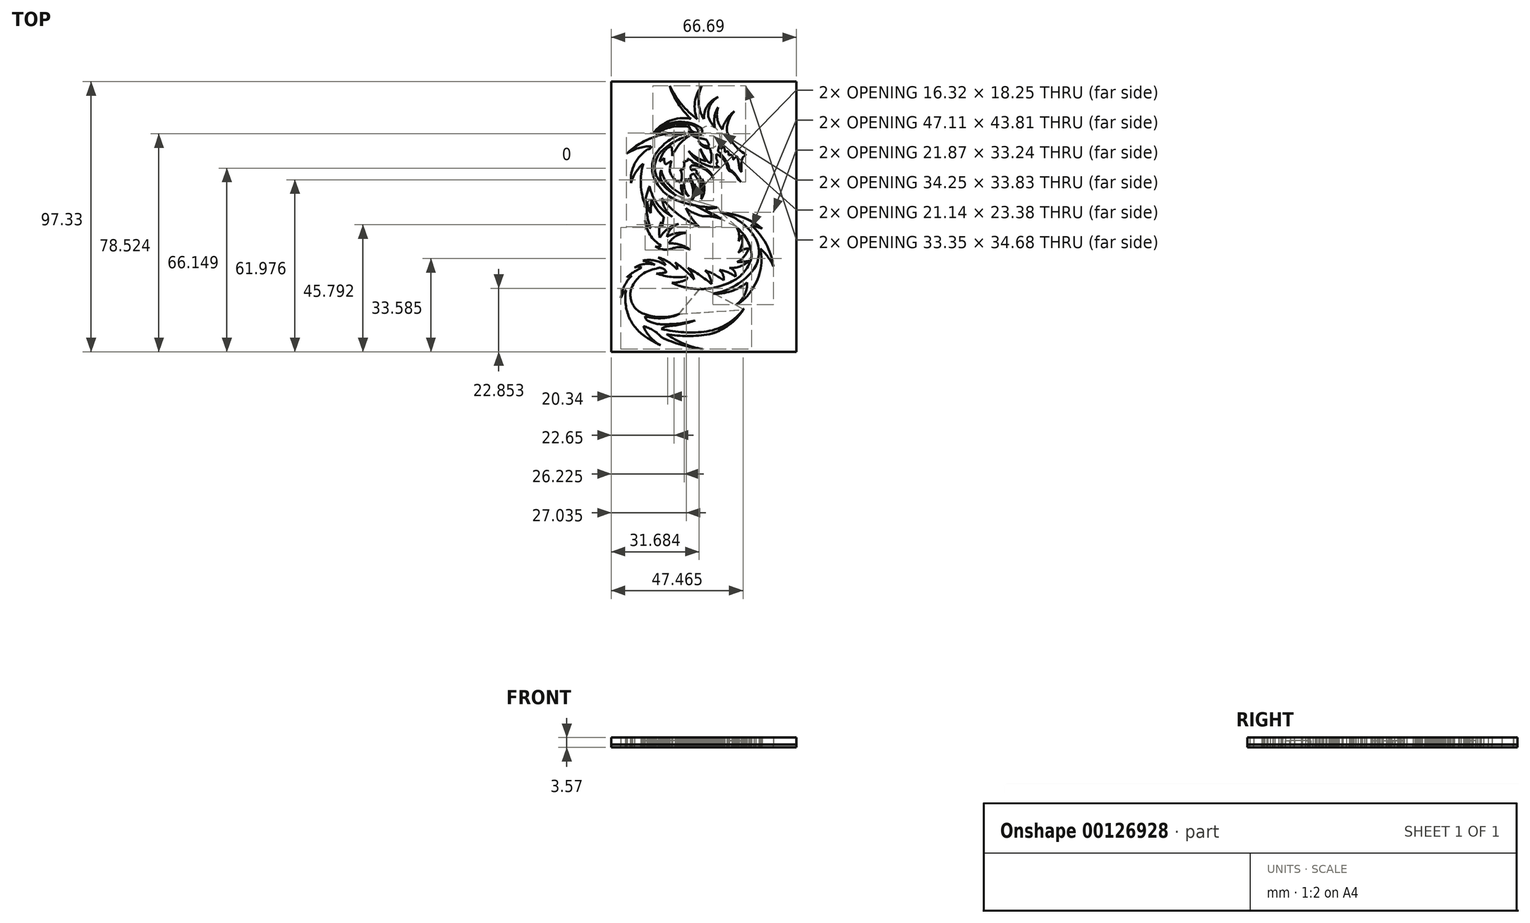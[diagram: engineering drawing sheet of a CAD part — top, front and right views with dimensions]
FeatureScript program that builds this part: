
annotation { "Feature Type Name" : "Feature", "Feature Type Description" : "" }
export const myFeature = defineFeature(function(context is Context, id is Id, definition is map)
    precondition{}
    {
        {
            var Q0;
            Q0=qCreatedBy(makeId("Top.planeOp"),FACE);
            var sketch = newSketch(context, id + "F0", { "sketchPlane" : qUnion([Q0])});
            skArc(sketch, "E0", {"start": v(-30.65, 39.22) * mm, "mid": v(-28.15, 34.33) * mm, "end": v(-23.98, 30.75) * mm});
            skArc(sketch, "E1", {"start": v(-27.91, 46.24) * mm, "mid": v(-29.97, 43) * mm, "end": v(-30.65, 39.22) * mm});
            skArc(sketch, "E2", {"start": v(-27.91, 46.24) * mm, "mid": v(-30.67, 43.35) * mm, "end": v(-32.32, 39.7) * mm});
            skArc(sketch, "E3", {"start": v(-33.8, 47.63) * mm, "mid": v(-34.11, 43.47) * mm, "end": v(-32.32, 39.7) * mm});
            skArc(sketch, "E4", {"start": v(-33.8, 47.63) * mm, "mid": v(-35.12, 44.08) * mm, "end": v(-34.92, 40.3) * mm});
            skArc(sketch, "E5", {"start": v(-37.4, 44.6) * mm, "mid": v(-36.44, 42.3) * mm, "end": v(-34.92, 40.3) * mm});
            skArc(sketch, "E6", {"start": v(-33.82, 51.28) * mm, "mid": v(-36.58, 48.47) * mm, "end": v(-37.4, 44.6) * mm});
            skArc(sketch, "E7", {"start": v(-33.82, 51.28) * mm, "mid": v(-37.67, 48.18) * mm, "end": v(-38.9, 43.4) * mm});
            skArc(sketch, "E8", {"start": v(-39.73, 55.3) * mm, "mid": v(-40.83, 49.25) * mm, "end": v(-38.9, 43.4) * mm});
            skArc(sketch, "E9", {"start": v(-39.73, 55.3) * mm, "mid": v(-42.15, 49.52) * mm, "end": v(-41.34, 43.3) * mm});
            skArc(sketch, "E10", {"start": v(-51.25, 55.4) * mm, "mid": v(-47, 48.77) * mm, "end": v(-41.34, 43.3) * mm});
            skArc(sketch, "E11", {"start": v(-51.25, 55.4) * mm, "mid": v(-48.2, 48.97) * mm, "end": v(-43.64, 43.52) * mm});
            skArc(sketch, "E12", {"start": v(-43.64, 43.52) * mm, "mid": v(-51.25, 42.81) * mm, "end": v(-57.28, 38.12) * mm});
            skArc(sketch, "E13", {"start": v(-40.35, 40.47) * mm, "mid": v(-49.23, 42.31) * mm, "end": v(-57.28, 38.12) * mm});
            skArc(sketch, "E14", {"start": v(-41.33, 37.48) * mm, "mid": v(-39.58, 38.56) * mm, "end": v(-40.35, 40.47) * mm});
            skArc(sketch, "E15", {"start": v(-44.38, 38.98) * mm, "mid": v(-42.91, 38.11) * mm, "end": v(-41.33, 37.48) * mm});
            skArc(sketch, "E16", {"start": v(-44.38, 38.98) * mm, "mid": v(-42.8, 37.4) * mm, "end": v(-40.77, 36.48) * mm});
            skArc(sketch, "E17", {"start": v(-37.91, 35.86) * mm, "mid": v(-39.31, 36.3) * mm, "end": v(-40.77, 36.48) * mm});
            skArc(sketch, "E18", {"start": v(-37.01, 33.75) * mm, "mid": v(-37.4, 34.83) * mm, "end": v(-37.91, 35.86) * mm});
            skArc(sketch, "E19", {"start": v(-40.85, 35.6) * mm, "mid": v(-39.24, 34.04) * mm, "end": v(-37.01, 33.75) * mm});
            skArc(sketch, "E20", {"start": v(-40.85, 35.6) * mm, "mid": v(-39.3, 33.56) * mm, "end": v(-36.83, 32.89) * mm});
            skArc(sketch, "E21", {"start": v(-44.1, 40.51) * mm, "mid": v(-50.54, 40.52) * mm, "end": v(-56.45, 37.97) * mm});
            skArc(sketch, "E22", {"start": v(-44.1, 40.51) * mm, "mid": v(-42.88, 38.87) * mm, "end": v(-40.83, 38.7) * mm});
            skArc(sketch, "E23", {"start": v(-40.83, 38.7) * mm, "mid": v(-41.92, 40.55) * mm, "end": v(-43.82, 41.54) * mm});
            skArc(sketch, "E24", {"start": v(-43.82, 41.54) * mm, "mid": v(-50.56, 41.26) * mm, "end": v(-56.45, 37.97) * mm});
            skArc(sketch, "E25", {"start": v(-36.45, 27.58) * mm, "mid": v(-36.2, 30.27) * mm, "end": v(-36.83, 32.89) * mm});
            skArc(sketch, "E26", {"start": v(-37.87, 28.52) * mm, "mid": v(-37.26, 27.9) * mm, "end": v(-36.45, 27.58) * mm});
            skArc(sketch, "E27", {"start": v(-40.23, 32.6) * mm, "mid": v(-39.08, 30.55) * mm, "end": v(-37.87, 28.52) * mm});
            skArc(sketch, "E28", {"start": v(-40.23, 32.6) * mm, "mid": v(-39.32, 30.32) * mm, "end": v(-38.12, 28.17) * mm});
            skArc(sketch, "E29", {"start": v(-44.48, 31.94) * mm, "mid": v(-41.56, 29.61) * mm, "end": v(-38.12, 28.17) * mm});
            skArc(sketch, "E30", {"start": v(-44.48, 31.94) * mm, "mid": v(-39.63, 27.52) * mm, "end": v(-33.25, 25.95) * mm});
            skLineSegment(sketch, "E31", {"start": v(-33.25, 25.95) * mm, "end": v(-34.39, 26.7) * mm});
            skLineSegment(sketch, "E32", {"start": v(-34.39, 26.7) * mm, "end": v(-34.17, 27.04) * mm});
            skLineSegment(sketch, "E33", {"start": v(-34.17, 27.04) * mm, "end": v(-34.49, 27.25) * mm});
            skLineSegment(sketch, "E34", {"start": v(-34.49, 27.25) * mm, "end": v(-33.88, 28.16) * mm});
            skLineSegment(sketch, "E35", {"start": v(-33.88, 28.16) * mm, "end": v(-34.5, 28.99) * mm});
            skLineSegment(sketch, "E36", {"start": v(-34.5, 28.99) * mm, "end": v(-34.5, 30.8) * mm});
            skArc(sketch, "E37", {"start": v(-30.56, 26.27) * mm, "mid": v(-32.03, 28.98) * mm, "end": v(-34.5, 30.8) * mm});
            skArc(sketch, "E38", {"start": v(-30.56, 26.27) * mm, "mid": v(-30.05, 25.03) * mm, "end": v(-28.88, 24.37) * mm});
            skArc(sketch, "E39", {"start": v(-26.66, 21.73) * mm, "mid": v(-27.64, 23.16) * mm, "end": v(-28.88, 24.37) * mm});
            skLineSegment(sketch, "E40", {"start": v(-26.66, 21.73) * mm, "end": v(-25.6, 20.73) * mm});
            skArc(sketch, "E41", {"start": v(-25.6, 20.73) * mm, "mid": v(-27.04, 22.77) * mm, "end": v(-28.66, 24.67) * mm});
            skArc(sketch, "E42", {"start": v(-30.06, 26.64) * mm, "mid": v(-29.68, 25.43) * mm, "end": v(-28.66, 24.67) * mm});
            skArc(sketch, "E43", {"start": v(-30.06, 26.64) * mm, "mid": v(-31.62, 29.41) * mm, "end": v(-33.8, 31.73) * mm});
            skArc(sketch, "E44", {"start": v(-33.24, 34.08) * mm, "mid": v(-33.64, 32.93) * mm, "end": v(-33.8, 31.73) * mm});
            skArc(sketch, "E45", {"start": v(-32.75, 32.61) * mm, "mid": v(-32.92, 33.37) * mm, "end": v(-33.24, 34.08) * mm});
            skArc(sketch, "E46", {"start": v(-31.8, 33.49) * mm, "mid": v(-32.29, 33.06) * mm, "end": v(-32.75, 32.61) * mm});
            skArc(sketch, "E47", {"start": v(-31.35, 31.52) * mm, "mid": v(-31.44, 32.54) * mm, "end": v(-31.8, 33.49) * mm});
            skArc(sketch, "E48", {"start": v(-30.2, 31.73) * mm, "mid": v(-30.8, 31.7) * mm, "end": v(-31.35, 31.52) * mm});
            skArc(sketch, "E49", {"start": v(-30.04, 30.38) * mm, "mid": v(-30.04, 31.07) * mm, "end": v(-30.2, 31.73) * mm});
            skArc(sketch, "E50", {"start": v(-28.88, 30.38) * mm, "mid": v(-29.46, 30.48) * mm, "end": v(-30.04, 30.38) * mm});
            skArc(sketch, "E51", {"start": v(-28.37, 28.76) * mm, "mid": v(-28.5, 29.61) * mm, "end": v(-28.88, 30.38) * mm});
            skArc(sketch, "E52", {"start": v(-28.37, 28.76) * mm, "mid": v(-27.87, 29.27) * mm, "end": v(-27.38, 29.8) * mm});
            skArc(sketch, "E53", {"start": v(-26.81, 29.56) * mm, "mid": v(-27.04, 29.83) * mm, "end": v(-27.38, 29.8) * mm});
            skArc(sketch, "E54", {"start": v(-26.23, 26.32) * mm, "mid": v(-26.48, 27.95) * mm, "end": v(-26.81, 29.56) * mm});
            skArc(sketch, "E55", {"start": v(-26.23, 26.32) * mm, "mid": v(-25.99, 25.22) * mm, "end": v(-25.35, 24.28) * mm});
            skArc(sketch, "E56", {"start": v(-25.1, 29.19) * mm, "mid": v(-25.46, 26.74) * mm, "end": v(-25.35, 24.28) * mm});
            skArc(sketch, "E57", {"start": v(-24.27, 30.17) * mm, "mid": v(-24.76, 29.74) * mm, "end": v(-25.1, 29.19) * mm});
            skArc(sketch, "E58", {"start": v(-24.27, 30.17) * mm, "mid": v(-23.97, 30.38) * mm, "end": v(-23.98, 30.75) * mm});
            skArc(sketch, "E59", {"start": v(-29.6, 33.27) * mm, "mid": v(-31.01, 36.2) * mm, "end": v(-33.51, 38.27) * mm});
            skArc(sketch, "E60", {"start": v(-29.6, 33.27) * mm, "mid": v(-31.1, 34.46) * mm, "end": v(-32.9, 35.15) * mm});
            skArc(sketch, "E61", {"start": v(-32.9, 35.15) * mm, "mid": v(-33.08, 36.73) * mm, "end": v(-33.51, 38.27) * mm});
            skArc(sketch, "E62", {"start": v(-44.07, 37.38) * mm, "mid": v(-49.23, 35.39) * mm, "end": v(-53.76, 32.2) * mm});
            skArc(sketch, "E63", {"start": v(-53.76, 32.2) * mm, "mid": v(-56.03, 29.04) * mm, "end": v(-56.6, 25.2) * mm});
            skArc(sketch, "E64", {"start": v(-56.6, 25.2) * mm, "mid": v(-55.99, 22.86) * mm, "end": v(-54.62, 20.88) * mm});
            skArc(sketch, "E65", {"start": v(-54.62, 20.88) * mm, "mid": v(-52.08, 18.07) * mm, "end": v(-48.97, 15.88) * mm});
            skArc(sketch, "E66", {"start": v(-54, 20.88) * mm, "mid": v(-51.62, 18.24) * mm, "end": v(-48.97, 15.88) * mm});
            skArc(sketch, "E67", {"start": v(-54.31, 25.05) * mm, "mid": v(-54.65, 22.93) * mm, "end": v(-54, 20.88) * mm});
            skArc(sketch, "E68", {"start": v(-54.31, 25.05) * mm, "mid": v(-53.52, 22.62) * mm, "end": v(-52.11, 20.49) * mm});
            skArc(sketch, "E69", {"start": v(-52.11, 20.49) * mm, "mid": v(-49.47, 17.9) * mm, "end": v(-46.27, 16.02) * mm});
            skArc(sketch, "E70", {"start": v(-47.1, 19.82) * mm, "mid": v(-47, 17.85) * mm, "end": v(-46.27, 16.02) * mm});
            skArc(sketch, "E71", {"start": v(-47.1, 19.82) * mm, "mid": v(-46.04, 17.46) * mm, "end": v(-44.33, 15.5) * mm});
            skArc(sketch, "E72", {"start": v(-46.1, 19.91) * mm, "mid": v(-45.63, 17.54) * mm, "end": v(-44.33, 15.5) * mm});
            skArc(sketch, "E73", {"start": v(-45.5, 21.93) * mm, "mid": v(-45.84, 20.93) * mm, "end": v(-46.1, 19.91) * mm});
            skArc(sketch, "E74", {"start": v(-44.98, 21.14) * mm, "mid": v(-45.23, 21.55) * mm, "end": v(-45.5, 21.93) * mm});
            skArc(sketch, "E75", {"start": v(-44.98, 21.14) * mm, "mid": v(-44.66, 21.54) * mm, "end": v(-44.33, 21.95) * mm});
            skArc(sketch, "E76", {"start": v(-43.3, 14) * mm, "mid": v(-42.86, 18.1) * mm, "end": v(-44.33, 21.95) * mm});
            skArc(sketch, "E77", {"start": v(-43.3, 14) * mm, "mid": v(-42.16, 16.91) * mm, "end": v(-42.28, 20.03) * mm});
            skArc(sketch, "E78", {"start": v(-42.64, 15.93) * mm, "mid": v(-42.28, 17.96) * mm, "end": v(-42.28, 20.03) * mm});
            skArc(sketch, "E79", {"start": v(-42.64, 15.93) * mm, "mid": v(-42.54, 19.02) * mm, "end": v(-43.58, 21.94) * mm});
            skArc(sketch, "E80", {"start": v(-43.58, 23.4) * mm, "mid": v(-43.71, 22.67) * mm, "end": v(-43.58, 21.94) * mm});
            skArc(sketch, "E81", {"start": v(-43.58, 23.4) * mm, "mid": v(-43.03, 23.5) * mm, "end": v(-42.5, 23.67) * mm});
            skArc(sketch, "E82", {"start": v(-39.85, 14.5) * mm, "mid": v(-40.19, 19.38) * mm, "end": v(-42.5, 23.67) * mm});
            skArc(sketch, "E83", {"start": v(-39.85, 14.5) * mm, "mid": v(-38.74, 18.16) * mm, "end": v(-39.58, 21.89) * mm});
            skArc(sketch, "E84", {"start": v(-39.2, 16.94) * mm, "mid": v(-39.09, 19.44) * mm, "end": v(-39.58, 21.89) * mm});
            skArc(sketch, "E85", {"start": v(-39.2, 16.94) * mm, "mid": v(-39.33, 19.35) * mm, "end": v(-40, 21.67) * mm});
            skArc(sketch, "E86", {"start": v(-40, 21.67) * mm, "mid": v(-40.65, 22.99) * mm, "end": v(-41.64, 24.08) * mm});
            skArc(sketch, "E87", {"start": v(-41.64, 24.08) * mm, "mid": v(-41.58, 24.45) * mm, "end": v(-41.64, 24.8) * mm});
            skLineSegment(sketch, "E88", {"start": v(-41.64, 24.8) * mm, "end": v(-42.69, 25.54) * mm});
            skLineSegment(sketch, "E89", {"start": v(-42.69, 25.54) * mm, "end": v(-43.1, 24.95) * mm});
            skArc(sketch, "E90", {"start": v(-43.61, 25.52) * mm, "mid": v(-43.5, 25.12) * mm, "end": v(-43.1, 24.95) * mm});
            skArc(sketch, "E91", {"start": v(-42.9, 26.75) * mm, "mid": v(-43.65, 26.36) * mm, "end": v(-43.61, 25.52) * mm});
            skArc(sketch, "E92", {"start": v(-35.5, 22.06) * mm, "mid": v(-38.63, 25.3) * mm, "end": v(-42.9, 26.75) * mm});
            skArc(sketch, "E93", {"start": v(-35.5, 22.06) * mm, "mid": v(-36.74, 24.3) * mm, "end": v(-38.86, 25.77) * mm});
            skArc(sketch, "E94", {"start": v(-38.86, 25.77) * mm, "mid": v(-40.86, 26.95) * mm, "end": v(-43.04, 27.76) * mm});
            skArc(sketch, "E95", {"start": v(-43.04, 27.76) * mm, "mid": v(-43.03, 28) * mm, "end": v(-43.04, 28.23) * mm});
            skArc(sketch, "E96", {"start": v(-43.04, 28.23) * mm, "mid": v(-43.9, 28.67) * mm, "end": v(-44.76, 29.1) * mm});
            skArc(sketch, "E97", {"start": v(-44.76, 28.4) * mm, "mid": v(-44.72, 28.75) * mm, "end": v(-44.76, 29.1) * mm});
            skArc(sketch, "E98", {"start": v(-46.2, 28.17) * mm, "mid": v(-45.47, 28.22) * mm, "end": v(-44.76, 28.4) * mm});
            skArc(sketch, "E99", {"start": v(-46.66, 25.12) * mm, "mid": v(-46.02, 26.58) * mm, "end": v(-46.2, 28.17) * mm});
            skArc(sketch, "E100", {"start": v(-47.34, 25.12) * mm, "mid": v(-47, 25.03) * mm, "end": v(-46.66, 25.12) * mm});
            skArc(sketch, "E101", {"start": v(-47.34, 20.54) * mm, "mid": v(-46.88, 22.83) * mm, "end": v(-47.34, 25.12) * mm});
            skArc(sketch, "E102", {"start": v(-51.2, 24.57) * mm, "mid": v(-49.8, 22.05) * mm, "end": v(-47.34, 20.54) * mm});
            skArc(sketch, "E103", {"start": v(-50.58, 28.31) * mm, "mid": v(-51.06, 26.47) * mm, "end": v(-51.2, 24.57) * mm});
            skArc(sketch, "E104", {"start": v(-50.58, 28.31) * mm, "mid": v(-51.46, 27.83) * mm, "end": v(-52.3, 27.29) * mm});
            skArc(sketch, "E105", {"start": v(-52.97, 27.29) * mm, "mid": v(-52.63, 27.2) * mm, "end": v(-52.3, 27.29) * mm});
            skArc(sketch, "E106", {"start": v(-53.23, 29.34) * mm, "mid": v(-53.2, 28.3) * mm, "end": v(-52.97, 27.29) * mm});
            skArc(sketch, "E107", {"start": v(-54.86, 28.12) * mm, "mid": v(-54.01, 28.68) * mm, "end": v(-53.23, 29.34) * mm});
            skArc(sketch, "E108", {"start": v(-52.71, 32.3) * mm, "mid": v(-54.04, 30.34) * mm, "end": v(-54.86, 28.12) * mm});
            skArc(sketch, "E109", {"start": v(-50.55, 33.43) * mm, "mid": v(-51.77, 33.13) * mm, "end": v(-52.71, 32.3) * mm});
            skArc(sketch, "E110", {"start": v(-50.3, 30.15) * mm, "mid": v(-50.38, 31.8) * mm, "end": v(-50.55, 33.43) * mm});
            skArc(sketch, "E111", {"start": v(-44.07, 37.38) * mm, "mid": v(-47.76, 34.26) * mm, "end": v(-50.3, 30.15) * mm});
            skArc(sketch, "E112", {"start": v(-45.67, 38.36) * mm, "mid": v(-57, 36.87) * mm, "end": v(-66.77, 30.92) * mm});
            skArc(sketch, "E113", {"start": v(-57.94, 33.58) * mm, "mid": v(-62.55, 32.91) * mm, "end": v(-66.77, 30.92) * mm});
            skArc(sketch, "E114", {"start": v(-58.97, 32.6) * mm, "mid": v(-58.21, 32.83) * mm, "end": v(-57.94, 33.58) * mm});
            skArc(sketch, "E115", {"start": v(-58.97, 32.6) * mm, "mid": v(-63.84, 27.36) * mm, "end": v(-65.15, 20.33) * mm});
            skArc(sketch, "E116", {"start": v(-60.7, 27.37) * mm, "mid": v(-63.48, 24.2) * mm, "end": v(-65.15, 20.33) * mm});
            skArc(sketch, "E117", {"start": v(-60.7, 27.37) * mm, "mid": v(-61.63, 19.86) * mm, "end": v(-60.06, 12.47) * mm});
            skArc(sketch, "E118", {"start": v(-58.46, 19.2) * mm, "mid": v(-59.6, 15.92) * mm, "end": v(-60.06, 12.47) * mm});
            skArc(sketch, "E119", {"start": v(-58.46, 19.2) * mm, "mid": v(-55.63, 12.78) * mm, "end": v(-50.33, 8.17) * mm});
            skArc(sketch, "E120", {"start": v(-54.03, 14.88) * mm, "mid": v(-52.9, 11.13) * mm, "end": v(-50.33, 8.17) * mm});
            skArc(sketch, "E121", {"start": v(-54.03, 14.88) * mm, "mid": v(-47.99, 8.91) * mm, "end": v(-40.67, 4.6) * mm});
            skArc(sketch, "E122", {"start": v(-45.41, 11.31) * mm, "mid": v(-43.35, 7.73) * mm, "end": v(-40.67, 4.6) * mm});
            skArc(sketch, "E123", {"start": v(-45.41, 11.31) * mm, "mid": v(-42.34, 9.47) * mm, "end": v(-38.93, 8.37) * mm});
            skArc(sketch, "E124", {"start": v(-32.51, 7.36) * mm, "mid": v(-35.67, 8.22) * mm, "end": v(-38.93, 8.37) * mm});
            skArc(sketch, "E125", {"start": v(-32.51, 7.36) * mm, "mid": v(-35.4, 9.06) * mm, "end": v(-38.47, 10.37) * mm});
            skLineSegment(sketch, "E126", {"start": v(-38.47, 10.37) * mm, "end": v(-37.48, 10.6) * mm});
            skLineSegment(sketch, "E127", {"start": v(-37.48, 10.6) * mm, "end": v(-38.38, 11) * mm});
            skArc(sketch, "E128", {"start": v(-38.38, 11) * mm, "mid": v(-36.3, 11.18) * mm, "end": v(-34.23, 11.53) * mm});
            skArc(sketch, "E129", {"start": v(-48.05, 13.84) * mm, "mid": v(-41.23, 12.13) * mm, "end": v(-34.23, 11.53) * mm});
            skArc(sketch, "E130", {"start": v(-57, 22.54) * mm, "mid": v(-53.46, 17.23) * mm, "end": v(-48.05, 13.84) * mm});
            skArc(sketch, "E131", {"start": v(-56.38, 30.7) * mm, "mid": v(-57.55, 26.69) * mm, "end": v(-57, 22.54) * mm});
            skArc(sketch, "E132", {"start": v(-45.67, 38.36) * mm, "mid": v(-51.74, 35.54) * mm, "end": v(-56.38, 30.7) * mm});
            skArc(sketch, "E133", {"start": v(-17.96, 3.97) * mm, "mid": v(-25.06, 8.04) * mm, "end": v(-33.07, 9.75) * mm});
            skArc(sketch, "E134", {"start": v(-17.96, 3.97) * mm, "mid": v(-19.96, 4.61) * mm, "end": v(-21.97, 5.23) * mm});
            skArc(sketch, "E135", {"start": v(-20.26, 0.3) * mm, "mid": v(-25.68, 6.35) * mm, "end": v(-33.07, 9.75) * mm});
            skArc(sketch, "E136", {"start": v(-20.8, -10.55) * mm, "mid": v(-19.11, -5.2) * mm, "end": v(-20.26, 0.3) * mm});
            skArc(sketch, "E137", {"start": v(-35.76, -19.51) * mm, "mid": v(-27.4, -16.51) * mm, "end": v(-20.8, -10.55) * mm});
            skArc(sketch, "E138", {"start": v(-35.76, -19.51) * mm, "mid": v(-29.16, -18.64) * mm, "end": v(-23.34, -15.42) * mm});
            skArc(sketch, "E139", {"start": v(-27.24, -23.5) * mm, "mid": v(-24.3, -19.93) * mm, "end": v(-23.34, -15.42) * mm});
            skArc(sketch, "E140", {"start": v(-27.24, -23.5) * mm, "mid": v(-24.36, -21.45) * mm, "end": v(-22.08, -18.75) * mm});
            skArc(sketch, "E141", {"start": v(-22.08, -18.75) * mm, "mid": v(-18.67, -11.4) * mm, "end": v(-18.62, -3.3) * mm});
            skArc(sketch, "E142", {"start": v(-13.89, -9.75) * mm, "mid": v(-15.88, -6.25) * mm, "end": v(-18.62, -3.3) * mm});
            skArc(sketch, "E143", {"start": v(-13.89, -9.75) * mm, "mid": v(-16.57, -1.53) * mm, "end": v(-21.97, 5.23) * mm});
            skArc(sketch, "E144", {"start": v(-21.7, -6.08) * mm, "mid": v(-23.29, -0.33) * mm, "end": v(-27.05, 4.3) * mm});
            skArc(sketch, "E145", {"start": v(-27.38, -14.33) * mm, "mid": v(-23.73, -10.76) * mm, "end": v(-21.7, -6.08) * mm});
            skArc(sketch, "E146", {"start": v(-50.47, -15.66) * mm, "mid": v(-38.76, -17.81) * mm, "end": v(-27.38, -14.33) * mm});
            skArc(sketch, "E147", {"start": v(-50.47, -15.66) * mm, "mid": v(-47.78, -15.3) * mm, "end": v(-45.2, -14.43) * mm});
            skArc(sketch, "E148", {"start": v(-45.2, -14.43) * mm, "mid": v(-45, -13.92) * mm, "end": v(-45.2, -13.42) * mm});
            skArc(sketch, "E149", {"start": v(-56.02, -12.25) * mm, "mid": v(-50.68, -13.48) * mm, "end": v(-45.2, -13.42) * mm});
            skArc(sketch, "E150", {"start": v(-56.02, -12.25) * mm, "mid": v(-54.2, -12.16) * mm, "end": v(-52.43, -11.8) * mm});
            skArc(sketch, "E151", {"start": v(-52.43, -11.8) * mm, "mid": v(-53.94, -10.34) * mm, "end": v(-56.04, -10.5) * mm});
            skArc(sketch, "E152", {"start": v(-56.04, -10.5) * mm, "mid": v(-61.13, -12.57) * mm, "end": v(-64.67, -16.8) * mm});
            skArc(sketch, "E153", {"start": v(-64.93, -13.02) * mm, "mid": v(-65.8, -13.2) * mm, "end": v(-66.63, -13.52) * mm});
            skArc(sketch, "E154", {"start": v(-61.33, -10.13) * mm, "mid": v(-64.09, -11.66) * mm, "end": v(-66.63, -13.52) * mm});
            skArc(sketch, "E155", {"start": v(-61.33, -10.13) * mm, "mid": v(-62.6, -9.8) * mm, "end": v(-63.86, -10.13) * mm});
            skArc(sketch, "E156", {"start": v(-56.58, -9.13) * mm, "mid": v(-60.33, -8.82) * mm, "end": v(-63.86, -10.13) * mm});
            skArc(sketch, "E157", {"start": v(-56.58, -9.13) * mm, "mid": v(-58.64, -8.21) * mm, "end": v(-60.84, -7.65) * mm});
            skArc(sketch, "E158", {"start": v(-52.77, -9.26) * mm, "mid": v(-56.63, -7.57) * mm, "end": v(-60.84, -7.65) * mm});
            skArc(sketch, "E159", {"start": v(-52.77, -9.26) * mm, "mid": v(-53.86, -7.63) * mm, "end": v(-55.42, -6.45) * mm});
            skArc(sketch, "E160", {"start": v(-48.6, -10.83) * mm, "mid": v(-51.66, -8.1) * mm, "end": v(-55.42, -6.45) * mm});
            skArc(sketch, "E161", {"start": v(-48.6, -10.83) * mm, "mid": v(-48.62, -9.47) * mm, "end": v(-49.25, -8.26) * mm});
            skArc(sketch, "E162", {"start": v(-42.47, -14.43) * mm, "mid": v(-45.68, -11.15) * mm, "end": v(-49.25, -8.26) * mm});
            skArc(sketch, "E163", {"start": v(-42.47, -14.43) * mm, "mid": v(-43.32, -12.15) * mm, "end": v(-44.78, -10.2) * mm});
            skArc(sketch, "E164", {"start": v(-36.14, -16.12) * mm, "mid": v(-40.3, -12.92) * mm, "end": v(-44.78, -10.2) * mm});
            skArc(sketch, "E165", {"start": v(-36.14, -16.12) * mm, "mid": v(-36.82, -13.4) * mm, "end": v(-38.5, -11.15) * mm});
            skArc(sketch, "E166", {"start": v(-31.8, -14.75) * mm, "mid": v(-35, -12.67) * mm, "end": v(-38.5, -11.15) * mm});
            skArc(sketch, "E167", {"start": v(-31.8, -14.75) * mm, "mid": v(-32.07, -12.65) * mm, "end": v(-33.36, -10.98) * mm});
            skArc(sketch, "E168", {"start": v(-27.57, -13.42) * mm, "mid": v(-30.3, -11.81) * mm, "end": v(-33.36, -10.98) * mm});
            skArc(sketch, "E169", {"start": v(-27.57, -13.42) * mm, "mid": v(-28, -11.34) * mm, "end": v(-29.8, -10.23) * mm});
            skArc(sketch, "E170", {"start": v(-26.9, -8.08) * mm, "mid": v(-24.76, -8.02) * mm, "end": v(-22.64, -7.7) * mm});
            skArc(sketch, "E171", {"start": v(-26.9, -8.08) * mm, "mid": v(-24.38, -6.06) * mm, "end": v(-22.81, -3.23) * mm});
            skArc(sketch, "E172", {"start": v(-22.81, -3.23) * mm, "mid": v(-24.84, -3.66) * mm, "end": v(-26.58, -4.8) * mm});
            skArc(sketch, "E173", {"start": v(-29.8, -10.23) * mm, "mid": v(-25.95, -9.73) * mm, "end": v(-22.64, -7.7) * mm});
            skArc(sketch, "E174", {"start": v(-26.58, -4.8) * mm, "mid": v(-25.17, -1.7) * mm, "end": v(-25.17, 1.7) * mm});
            skArc(sketch, "E175", {"start": v(-26.45, -0.58) * mm, "mid": v(-25.71, 0.5) * mm, "end": v(-25.17, 1.7) * mm});
            skArc(sketch, "E176", {"start": v(-26.45, -0.58) * mm, "mid": v(-26.27, 1.92) * mm, "end": v(-27.05, 4.3) * mm});
            skArc(sketch, "E177", {"start": v(-57.73, 14.46) * mm, "mid": v(-55.92, 10.98) * mm, "end": v(-53.36, 8) * mm});
            skArc(sketch, "E178", {"start": v(-53.36, 8) * mm, "mid": v(-53.68, 6.3) * mm, "end": v(-53.92, 4.56) * mm});
            skArc(sketch, "E179", {"start": v(-54.26, 6.36) * mm, "mid": v(-54.17, 5.45) * mm, "end": v(-53.92, 4.56) * mm});
            skArc(sketch, "E180", {"start": v(-54.26, 6.36) * mm, "mid": v(-55.04, 3.55) * mm, "end": v(-54.77, 0.65) * mm});
            skArc(sketch, "E181", {"start": v(-57.73, 14.46) * mm, "mid": v(-58, 12.01) * mm, "end": v(-58.13, 9.56) * mm});
            skArc(sketch, "E182", {"start": v(-59.31, 13.7) * mm, "mid": v(-59, 11.55) * mm, "end": v(-58.13, 9.56) * mm});
            skArc(sketch, "E183", {"start": v(-59.31, 13.7) * mm, "mid": v(-59.34, 8.8) * mm, "end": v(-58.1, 4.06) * mm});
            skArc(sketch, "E184", {"start": v(-60.11, 6.84) * mm, "mid": v(-59.35, 5.27) * mm, "end": v(-58.1, 4.06) * mm});
            skArc(sketch, "E185", {"start": v(-60.11, 6.84) * mm, "mid": v(-58.3, 1.67) * mm, "end": v(-54.37, -2.13) * mm});
            skArc(sketch, "E186", {"start": v(-56.39, -2.48) * mm, "mid": v(-55.31, -2.69) * mm, "end": v(-54.37, -2.13) * mm});
            skArc(sketch, "E187", {"start": v(-56.39, -2.48) * mm, "mid": v(-53.4, -3.64) * mm, "end": v(-50.23, -3.2) * mm});
            skArc(sketch, "E188", {"start": v(-43.8, -3.8) * mm, "mid": v(-46.94, -2.78) * mm, "end": v(-50.23, -3.2) * mm});
            skArc(sketch, "E189", {"start": v(-43.8, -3.8) * mm, "mid": v(-47.47, -1.89) * mm, "end": v(-51.58, -1.4) * mm});
            skArc(sketch, "E190", {"start": v(-45.22, 2.4) * mm, "mid": v(-48.87, 1.28) * mm, "end": v(-51.58, -1.4) * mm});
            skArc(sketch, "E191", {"start": v(-45.22, 2.4) * mm, "mid": v(-48.85, 2.26) * mm, "end": v(-52.25, 0.97) * mm});
            skArc(sketch, "E192", {"start": v(-48.04, 5.67) * mm, "mid": v(-50.78, 3.89) * mm, "end": v(-52.25, 0.97) * mm});
            skArc(sketch, "E193", {"start": v(-48.04, 5.67) * mm, "mid": v(-51.93, 3.88) * mm, "end": v(-54.77, 0.65) * mm});
            skArc(sketch, "E194", {"start": v(-64.93, -13.02) * mm, "mid": v(-67.55, -16.69) * mm, "end": v(-68.81, -21) * mm});
            skArc(sketch, "E195", {"start": v(-67, -18.3) * mm, "mid": v(-68.09, -19.53) * mm, "end": v(-68.81, -21) * mm});
            skArc(sketch, "E196", {"start": v(-67, -18.3) * mm, "mid": v(-67.1, -23.34) * mm, "end": v(-65.75, -28.2) * mm});
            skArc(sketch, "E197", {"start": v(-65.75, -28.2) * mm, "mid": v(-63.17, -32.24) * mm, "end": v(-59.52, -35.34) * mm});
            skArc(sketch, "E198", {"start": v(-59.52, -35.34) * mm, "mid": v(-57.05, -36.8) * mm, "end": v(-54.52, -38.12) * mm});
            skArc(sketch, "E199", {"start": v(-60.67, -31.23) * mm, "mid": v(-58.2, -35.23) * mm, "end": v(-54.52, -38.12) * mm});
            skArc(sketch, "E200", {"start": v(-54.2, -35.2) * mm, "mid": v(-57.15, -32.75) * mm, "end": v(-60.67, -31.23) * mm});
            skArc(sketch, "E201", {"start": v(-54.2, -35.2) * mm, "mid": v(-47, -37.98) * mm, "end": v(-39.42, -39.51) * mm});
            skArc(sketch, "E202", {"start": v(-52.36, -34.16) * mm, "mid": v(-46.18, -37.54) * mm, "end": v(-39.42, -39.51) * mm});
            skArc(sketch, "E203", {"start": v(-52.36, -34.16) * mm, "mid": v(-44.67, -34.79) * mm, "end": v(-36.98, -34.16) * mm});
            skArc(sketch, "E204", {"start": v(-36.98, -34.16) * mm, "mid": v(-29.87, -30.77) * mm, "end": v(-24.56, -24.94) * mm});
            skArc(sketch, "E205", {"start": v(-37.85, -33.11) * mm, "mid": v(-30.4, -30.33) * mm, "end": v(-24.56, -24.94) * mm});
            skArc(sketch, "E206", {"start": v(-54.2, -32.24) * mm, "mid": v(-46.07, -33.43) * mm, "end": v(-37.85, -33.11) * mm});
            skArc(sketch, "E207", {"start": v(-51.52, -31.2) * mm, "mid": v(-52.95, -31.5) * mm, "end": v(-54.2, -32.24) * mm});
            skArc(sketch, "E208", {"start": v(-51.52, -31.2) * mm, "mid": v(-46.7, -30.52) * mm, "end": v(-42.03, -29.15) * mm});
            skArc(sketch, "E209", {"start": v(-52.7, -30.54) * mm, "mid": v(-47.32, -30.2) * mm, "end": v(-42.03, -29.15) * mm});
            skArc(sketch, "E210", {"start": v(-59.42, -29.11) * mm, "mid": v(-56.17, -30.31) * mm, "end": v(-52.7, -30.54) * mm});
            skArc(sketch, "E211", {"start": v(-60.12, -27.72) * mm, "mid": v(-59.89, -28.48) * mm, "end": v(-59.42, -29.11) * mm});
            skArc(sketch, "E212", {"start": v(-60.12, -27.72) * mm, "mid": v(-53.77, -28.33) * mm, "end": v(-47.6, -26.78) * mm});
            skArc(sketch, "E213", {"start": v(-60.5, -26.78) * mm, "mid": v(-54.05, -27.97) * mm, "end": v(-47.6, -26.78) * mm});
            skArc(sketch, "E214", {"start": v(-65.33, -20.62) * mm, "mid": v(-63.86, -24.44) * mm, "end": v(-60.5, -26.78) * mm});
            skArc(sketch, "E215", {"start": v(-64.67, -16.8) * mm, "mid": v(-65.32, -18.65) * mm, "end": v(-65.33, -20.62) * mm});
            skLineSegment(sketch, "E216.bottom", {"start": v(-72.3, -40.46) * mm, "end": v(-5.6, -40.46) * mm});
            skLineSegment(sketch, "E216.top", {"start": v(-72.3, 56.87) * mm, "end": v(-5.6, 56.87) * mm});
            skLineSegment(sketch, "E216.left", {"start": v(-72.3, -40.46) * mm, "end": v(-72.3, 56.87) * mm});
            skLineSegment(sketch, "E216.right", {"start": v(-5.6, -40.46) * mm, "end": v(-5.6, 56.87) * mm});
            skSolve(sketch);
        }
        {
            var Q0;
            Q0=qSketchRegion(id+"F0",true);
            extrude(context, id + "F1", {"entities" : qUnion([Q0]), "depth" : 2.54 * mm});
        }
        {
            var Q0;
            Q0=qCreatedBy(makeId("Top.planeOp"),FACE);
            var sketch = newSketch(context, id + "F2", { "sketchPlane" : qUnion([Q0])});
            skLineSegment(sketch, "E217", {"start": v(-48.95, 15.98) * mm, "end": v(-33.78, 11.6) * mm});
            skLineSegment(sketch, "E218", {"start": v(-44.36, 37.37) * mm, "end": v(-45.76, 37.77) * mm});
            skLineSegment(sketch, "E219", {"start": v(-32.8, 9.8) * mm, "end": v(-33.78, 11.6) * mm});
            skLineSegment(sketch, "E220", {"start": v(-58.59, 14.23) * mm, "end": v(-60.62, 11.9) * mm});
            skLineSegment(sketch, "E221", {"start": v(-58.59, 14.23) * mm, "end": v(-56.95, 12.8) * mm});
            skLineSegment(sketch, "E222", {"start": v(-35.36, -19.45) * mm, "end": v(-40.38, -17.63) * mm});
            skLineSegment(sketch, "E223", {"start": v(-27.13, 4.57) * mm, "end": v(-32.8, 9.8) * mm});
            skLineSegment(sketch, "E224", {"start": v(-45.76, 37.77) * mm, "end": v(-48.7, 37.77) * mm});
            skLineSegment(sketch, "E225", {"start": v(-48.7, 37.77) * mm, "end": v(-55.6, 39.36) * mm});
            skLineSegment(sketch, "E226", {"start": v(-27.13, 4.57) * mm, "end": v(-34.03, 7.9) * mm});
            skLineSegment(sketch, "E227", {"start": v(-34.03, 7.9) * mm, "end": v(-48.95, 15.98) * mm});
            skLineSegment(sketch, "E228", {"start": v(-40.38, -17.63) * mm, "end": v(-35.36, -19.45) * mm});
            skLineSegment(sketch, "E229", {"start": v(-35.36, -19.45) * mm, "end": v(-27.81, -23.4) * mm});
            skLineSegment(sketch, "E230", {"start": v(-27.81, -23.4) * mm, "end": v(-24.58, -25.28) * mm});
            skLineSegment(sketch, "E231", {"start": v(-44.36, 37.37) * mm, "end": v(-44.36, 41.7) * mm});
            skLineSegment(sketch, "E232", {"start": v(-44.36, 41.7) * mm, "end": v(-55.6, 39.36) * mm});
            skLineSegment(sketch, "E233", {"start": v(-55.6, 39.36) * mm, "end": v(-44.36, 41.7) * mm});
            skLineSegment(sketch, "E234", {"start": v(-60.62, 11.9) * mm, "end": v(-56.95, 12.8) * mm});
            skLineSegment(sketch, "E235", {"start": v(-40.38, -17.63) * mm, "end": v(-48.05, -26.84) * mm});
            skLineSegment(sketch, "E236", {"start": v(-48.05, -26.84) * mm, "end": v(-24.58, -25.28) * mm});
            skSolve(sketch);
        }
        {
            var Q0;
            Q0 = qSketchRegion(id + "F2", true);
            extrude(context, id + "F3", {"entities" : qUnion([Q0]), "depth" : 1.4 * mm});
        }
        {
            var Q0;
            Q0 = qSketchRegion(id + "F0", true);
            extrude(context, id + "F4", {"entities" : qUnion([Q0]), "oppositeDirection" : true, "depth" : 1.03 * mm});
        }
    });
